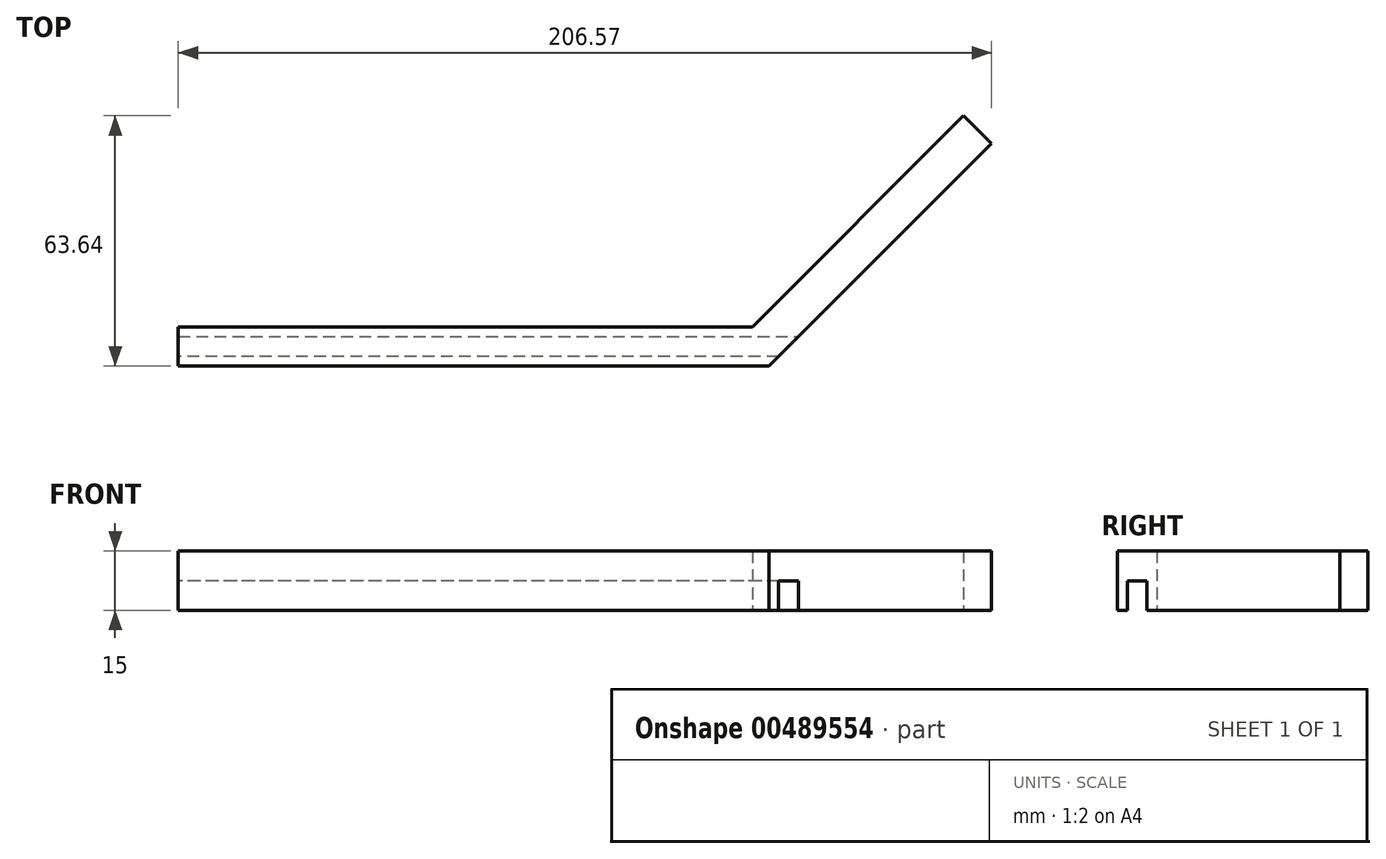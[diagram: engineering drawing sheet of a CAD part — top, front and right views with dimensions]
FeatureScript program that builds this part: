
annotation { "Feature Type Name" : "Feature", "Feature Type Description" : "" }
export const myFeature = defineFeature(function(context is Context, id is Id, definition is map)
    precondition{}
    {
        {
            var Q0;
            Q0=qCreatedBy(makeId("Top.planeOp"),FACE);
            var sketch = newSketch(context, id + "F0", { "sketchPlane" : qUnion([Q0])});
            skLineSegment(sketch, "E0", {"start": v(70.6, 0) * mm, "end": v(14.03, -56.57) * mm});
            skLineSegment(sketch, "E1", {"start": v(14.03, -56.57) * mm, "end": v(-135.97, -56.57) * mm});
            skLineSegment(sketch, "E2.0", {"start": v(9.89, -46.57) * mm, "end": v(-110.18, -46.57) * mm});
            skLineSegment(sketch, "E2.1", {"start": v(36.45, -20) * mm, "end": v(9.89, -46.57) * mm});
            skLineSegment(sketch, "E3", {"start": v(-110.18, -46.57) * mm, "end": v(-135.97, -46.57) * mm});
            skLineSegment(sketch, "E4", {"start": v(36.45, -20) * mm, "end": v(63.52, 7.07) * mm});
            skLineSegment(sketch, "E5", {"start": v(63.52, 7.07) * mm, "end": v(70.6, 0) * mm});
            skLineSegment(sketch, "E6", {"start": v(-135.97, -46.57) * mm, "end": v(-135.97, -56.57) * mm});
            skSolve(sketch);
        }
        {
            var Q0;
            Q0=makeQuery(id+"F0.imprint","IMPRINT",FACE,{"disambiguationData":[TD([[makeQuery(id+"F0.imprint","IMPRINT",EDGE,{"derivedFrom":sQuery(id+"F0.wireOp",EDGE,"E0")}),-1.0]])]});
            extrude(context, id + "F1", {"entities" : qUnion([Q0]), "depth" : 15 * mm});
        }
        {
            var Q0;
            Q0=makeQuery(id+"F1.opExtrude","SWEPT_FACE",FACE,{"disambiguationData":[OSD([sQuery(id+"F0.wireOp",EDGE,"E6")])]});
            var sketch = newSketch(context, id + "F2", { "sketchPlane" : qUnion([Q0])});
            skLineSegment(sketch, "E7.bottom", {"start": v(54.07, 7.5) * mm, "end": v(49.07, 7.5) * mm});
            skLineSegment(sketch, "E7.left", {"start": v(54.07, 7.5) * mm, "end": v(54.07, 0) * mm});
            skLineSegment(sketch, "E7.right", {"start": v(49.07, 7.5) * mm, "end": v(49.07, 0) * mm});
            skPoint(sketch, "E7.middle", {"position": v(51.57, 0) * mm});
            skLineSegment(sketch, "E8", {"start": v(49.07, 0) * mm, "end": v(54.07, 0) * mm});
            skPoint(sketch, "E7.top.end.orphan", {"position": v(49.07, -7.5) * mm});
            skPoint(sketch, "E7.top.start.orphan", {"position": v(54.07, -7.5) * mm});
            skLineSegment(sketch, "E9", {"start": v(46.57, 15) * mm, "end": v(56.57, 15) * mm});
            skSolve(sketch);
        }
        {
            var Q0;
            Q0 = qSketchRegion(id + "F2", true);
            extrude(context, id + "F3", {"entities" : qUnion([Q0]), "operationType" : NewBodyOperationType.REMOVE, "endBound" : BoundingType.THROUGH_ALL, "oppositeDirection" : true, "depth" : 150 * mm});
        }
    });
